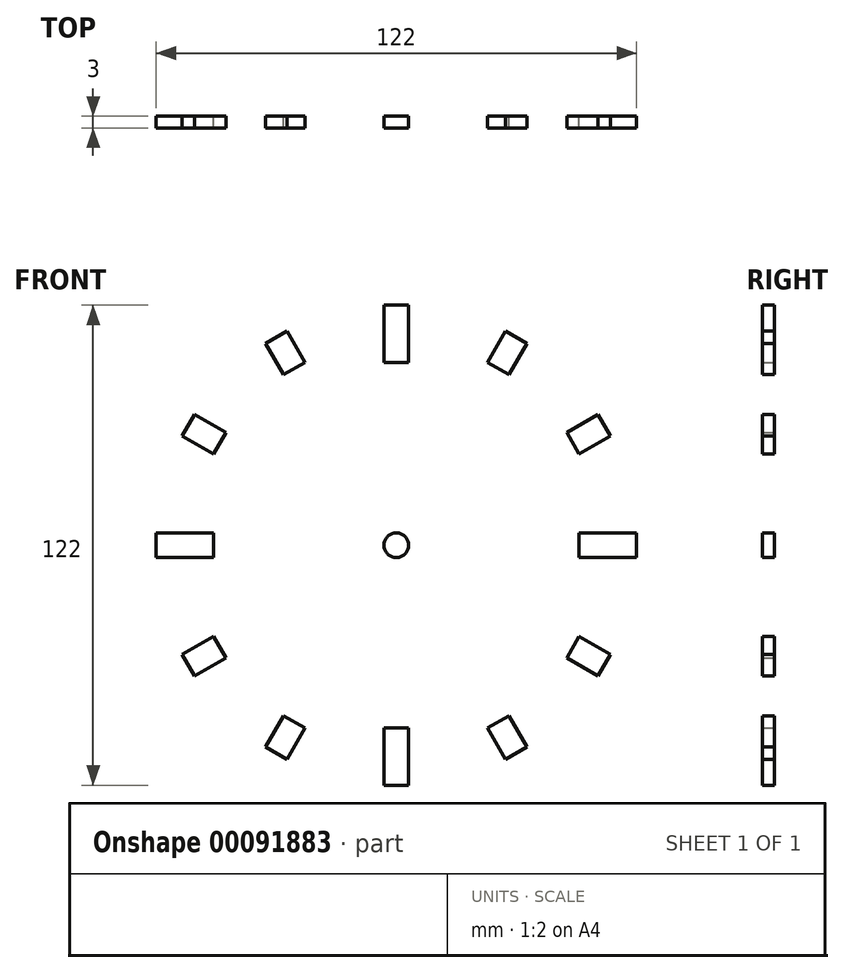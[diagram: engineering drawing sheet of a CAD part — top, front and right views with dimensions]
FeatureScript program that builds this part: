
annotation { "Feature Type Name" : "Feature", "Feature Type Description" : "" }
export const myFeature = defineFeature(function(context is Context, id is Id, definition is map)
    precondition{}
    {
        {
            var Q0;
            Q0=qCreatedBy(makeId("Front.planeOp"),FACE);
            var sketch = newSketch(context, id + "F0", { "sketchPlane" : qUnion([Q0])});
            skLineSegment(sketch, "E0.bottom", {"start": v(3.13, 51.82) * mm, "end": v(-3.13, 51.82) * mm});
            skLineSegment(sketch, "E0.top", {"start": v(3.13, 61) * mm, "end": v(-3.13, 61) * mm});
            skLineSegment(sketch, "E0.left", {"start": v(3.13, 51.82) * mm, "end": v(3.13, 61) * mm});
            skLineSegment(sketch, "E0.right", {"start": v(-3.13, 51.82) * mm, "end": v(-3.13, 61) * mm});
            skPoint(sketch, "E0.middle", {"position": v(0, 56.41) * mm});
            skLineSegment(sketch, "E1.1.0", {"start": v(-28.62, 43.31) * mm, "end": v(-33.21, 51.26) * mm});
            skLineSegment(sketch, "E1.1.1", {"start": v(-27.79, 54.4) * mm, "end": v(-33.21, 51.26) * mm});
            skLineSegment(sketch, "E1.1.2", {"start": v(-23.2, 46.44) * mm, "end": v(-27.79, 54.4) * mm});
            skLineSegment(sketch, "E1.1.3", {"start": v(-23.2, 46.44) * mm, "end": v(-28.62, 43.31) * mm});
            skLineSegment(sketch, "E1.2.0", {"start": v(-46.44, 23.2) * mm, "end": v(-54.4, 27.79) * mm});
            skLineSegment(sketch, "E1.2.1", {"start": v(-51.26, 33.21) * mm, "end": v(-54.4, 27.79) * mm});
            skLineSegment(sketch, "E1.2.2", {"start": v(-43.31, 28.62) * mm, "end": v(-51.26, 33.21) * mm});
            skLineSegment(sketch, "E1.2.3", {"start": v(-43.31, 28.62) * mm, "end": v(-46.44, 23.2) * mm});
            skPoint(sketch, "E1.center", {"position": v(0, 0) * mm});
            skLineSegment(sketch, "E2.1.3.0", {"start": v(-51.82, -3.13) * mm, "end": v(-61, -3.13) * mm});
            skLineSegment(sketch, "E2.3.3.0", {"start": v(-61, 3.13) * mm, "end": v(-61, -3.13) * mm});
            skLineSegment(sketch, "E2.6.3.0", {"start": v(-51.82, 3.13) * mm, "end": v(-61, 3.13) * mm});
            skLineSegment(sketch, "E2.9.3.0", {"start": v(-51.82, 3.13) * mm, "end": v(-51.82, -3.13) * mm});
            skLineSegment(sketch, "E2.1.4.0", {"start": v(-43.31, -28.62) * mm, "end": v(-51.26, -33.21) * mm});
            skLineSegment(sketch, "E2.3.4.0", {"start": v(-54.4, -27.79) * mm, "end": v(-51.26, -33.21) * mm});
            skLineSegment(sketch, "E2.6.4.0", {"start": v(-46.44, -23.2) * mm, "end": v(-54.4, -27.79) * mm});
            skLineSegment(sketch, "E2.9.4.0", {"start": v(-46.44, -23.2) * mm, "end": v(-43.31, -28.62) * mm});
            skLineSegment(sketch, "E2.1.5.0", {"start": v(-23.2, -46.44) * mm, "end": v(-27.79, -54.4) * mm});
            skLineSegment(sketch, "E2.3.5.0", {"start": v(-33.21, -51.26) * mm, "end": v(-27.79, -54.4) * mm});
            skLineSegment(sketch, "E2.6.5.0", {"start": v(-28.62, -43.31) * mm, "end": v(-33.21, -51.26) * mm});
            skLineSegment(sketch, "E2.9.5.0", {"start": v(-28.62, -43.31) * mm, "end": v(-23.2, -46.44) * mm});
            skLineSegment(sketch, "E2.1.6.0", {"start": v(3.13, -51.82) * mm, "end": v(3.13, -61) * mm});
            skLineSegment(sketch, "E2.3.6.0", {"start": v(-3.13, -61) * mm, "end": v(3.13, -61) * mm});
            skLineSegment(sketch, "E2.6.6.0", {"start": v(-3.13, -51.82) * mm, "end": v(-3.13, -61) * mm});
            skLineSegment(sketch, "E2.9.6.0", {"start": v(-3.13, -51.82) * mm, "end": v(3.13, -51.82) * mm});
            skLineSegment(sketch, "E2.1.7.0", {"start": v(28.62, -43.31) * mm, "end": v(33.21, -51.26) * mm});
            skLineSegment(sketch, "E2.3.7.0", {"start": v(27.79, -54.4) * mm, "end": v(33.21, -51.26) * mm});
            skLineSegment(sketch, "E2.6.7.0", {"start": v(23.2, -46.44) * mm, "end": v(27.79, -54.4) * mm});
            skLineSegment(sketch, "E2.9.7.0", {"start": v(23.2, -46.44) * mm, "end": v(28.62, -43.31) * mm});
            skLineSegment(sketch, "E2.1.8.0", {"start": v(46.44, -23.2) * mm, "end": v(54.4, -27.79) * mm});
            skLineSegment(sketch, "E2.3.8.0", {"start": v(51.26, -33.21) * mm, "end": v(54.4, -27.79) * mm});
            skLineSegment(sketch, "E2.6.8.0", {"start": v(43.31, -28.62) * mm, "end": v(51.26, -33.21) * mm});
            skLineSegment(sketch, "E2.9.8.0", {"start": v(43.31, -28.62) * mm, "end": v(46.44, -23.2) * mm});
            skLineSegment(sketch, "E2.1.9.0", {"start": v(51.82, 3.13) * mm, "end": v(61, 3.13) * mm});
            skLineSegment(sketch, "E2.3.9.0", {"start": v(61, -3.13) * mm, "end": v(61, 3.13) * mm});
            skLineSegment(sketch, "E2.6.9.0", {"start": v(51.82, -3.13) * mm, "end": v(61, -3.13) * mm});
            skLineSegment(sketch, "E2.9.9.0", {"start": v(51.82, -3.13) * mm, "end": v(51.82, 3.13) * mm});
            skLineSegment(sketch, "E2.1.10.0", {"start": v(43.31, 28.62) * mm, "end": v(51.26, 33.21) * mm});
            skLineSegment(sketch, "E2.3.10.0", {"start": v(54.4, 27.79) * mm, "end": v(51.26, 33.21) * mm});
            skLineSegment(sketch, "E2.6.10.0", {"start": v(46.44, 23.2) * mm, "end": v(54.4, 27.79) * mm});
            skLineSegment(sketch, "E2.9.10.0", {"start": v(46.44, 23.2) * mm, "end": v(43.31, 28.62) * mm});
            skLineSegment(sketch, "E2.1.11.0", {"start": v(23.2, 46.44) * mm, "end": v(27.79, 54.4) * mm});
            skLineSegment(sketch, "E2.3.11.0", {"start": v(33.21, 51.26) * mm, "end": v(27.79, 54.4) * mm});
            skLineSegment(sketch, "E2.6.11.0", {"start": v(28.62, 43.31) * mm, "end": v(33.21, 51.26) * mm});
            skLineSegment(sketch, "E2.9.11.0", {"start": v(28.62, 43.31) * mm, "end": v(23.2, 46.44) * mm});
            skLineSegment(sketch, "E3.bottom", {"start": v(-3.13, 51.82) * mm, "end": v(3.13, 51.82) * mm});
            skLineSegment(sketch, "E3.top", {"start": v(-3.13, 46.44) * mm, "end": v(3.13, 46.44) * mm});
            skLineSegment(sketch, "E3.left", {"start": v(-3.13, 51.82) * mm, "end": v(-3.13, 46.44) * mm});
            skLineSegment(sketch, "E3.right", {"start": v(3.13, 51.82) * mm, "end": v(3.13, 46.44) * mm});
            skLineSegment(sketch, "E4.1.0", {"start": v(-51.82, -3.13) * mm, "end": v(-51.82, 3.13) * mm});
            skLineSegment(sketch, "E4.1.1", {"start": v(-51.82, 3.13) * mm, "end": v(-46.44, 3.13) * mm});
            skLineSegment(sketch, "E4.1.2", {"start": v(-46.44, -3.13) * mm, "end": v(-46.44, 3.13) * mm});
            skLineSegment(sketch, "E4.1.3", {"start": v(-51.82, -3.13) * mm, "end": v(-46.44, -3.13) * mm});
            skLineSegment(sketch, "E4.2.0", {"start": v(3.13, -51.82) * mm, "end": v(-3.13, -51.82) * mm});
            skLineSegment(sketch, "E4.2.1", {"start": v(-3.13, -51.82) * mm, "end": v(-3.13, -46.44) * mm});
            skLineSegment(sketch, "E4.2.2", {"start": v(3.13, -46.44) * mm, "end": v(-3.13, -46.44) * mm});
            skLineSegment(sketch, "E4.2.3", {"start": v(3.13, -51.82) * mm, "end": v(3.13, -46.44) * mm});
            skLineSegment(sketch, "E4.3.0", {"start": v(51.82, 3.13) * mm, "end": v(51.82, -3.13) * mm});
            skLineSegment(sketch, "E4.3.1", {"start": v(51.82, -3.13) * mm, "end": v(46.44, -3.13) * mm});
            skLineSegment(sketch, "E4.3.2", {"start": v(46.44, 3.13) * mm, "end": v(46.44, -3.13) * mm});
            skLineSegment(sketch, "E4.3.3", {"start": v(51.82, 3.13) * mm, "end": v(46.44, 3.13) * mm});
            skCircle(sketch, "E5", {"center": v(0, 0) * mm, "radius": 3.13 * mm});
            skSolve(sketch);
        }
        {
            var Q0;
            Q0 = qSketchRegion(id + "F0", true);
            extrude(context, id + "F1", {"entities" : qUnion([Q0]), "depth" : 3 * mm});
        }
    });
